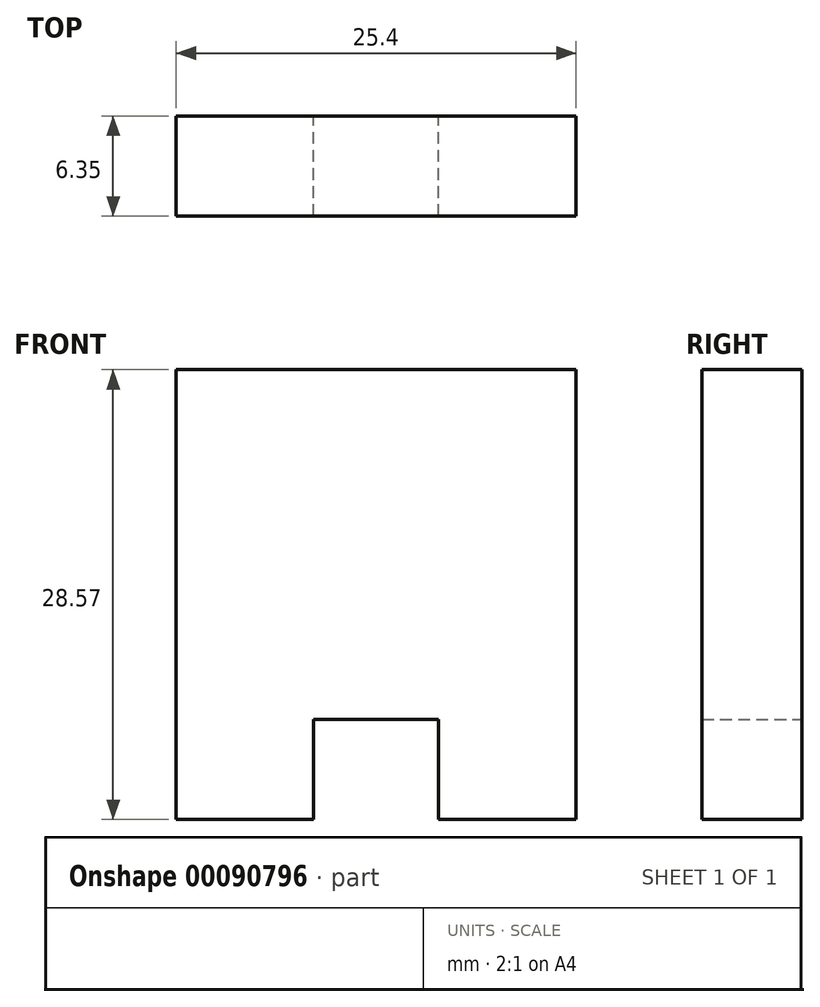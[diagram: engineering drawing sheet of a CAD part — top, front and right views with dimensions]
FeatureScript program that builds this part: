
annotation { "Feature Type Name" : "Feature", "Feature Type Description" : "" }
export const myFeature = defineFeature(function(context is Context, id is Id, definition is map)
    precondition{}
    {
        {
            var Q0;
            Q0=qCreatedBy(makeId("Front.planeOp"),FACE);
            var sketch = newSketch(context, id + "F0", { "sketchPlane" : qUnion([Q0])});
            skLineSegment(sketch, "E0.bottom", {"start": v(0, 0) * mm, "end": v(25.4, 0) * mm});
            skLineSegment(sketch, "E0.top", {"start": v(0, -28.57) * mm, "end": v(25.4, -28.57) * mm});
            skLineSegment(sketch, "E0.left", {"start": v(0, 0) * mm, "end": v(0, -28.57) * mm});
            skLineSegment(sketch, "E0.right", {"start": v(25.4, 0) * mm, "end": v(25.4, -28.57) * mm});
            skLineSegment(sketch, "E1.bottom", {"start": v(12.7, -28.57) * mm, "end": v(8.73, -28.57) * mm});
            skLineSegment(sketch, "E1.top", {"start": v(12.7, -22.22) * mm, "end": v(8.73, -22.22) * mm});
            skLineSegment(sketch, "E1.left", {"start": v(12.7, -28.57) * mm, "end": v(12.7, -22.22) * mm});
            skLineSegment(sketch, "E1.right", {"start": v(8.73, -28.57) * mm, "end": v(8.73, -22.22) * mm});
            skLineSegment(sketch, "E2.MirrorCS", {"start": v(12.7, -22.22) * mm, "end": v(16.67, -22.22) * mm});
            skLineSegment(sketch, "E3.MirrorCS", {"start": v(16.67, -28.57) * mm, "end": v(16.67, -22.22) * mm});
            skLineSegment(sketch, "E4.MirrorCS", {"start": v(12.7, -28.57) * mm, "end": v(16.67, -28.57) * mm});
            skSolve(sketch);
        }
        {
            var Q0;
            Q0=makeQuery(id+"F0.imprint","IMPRINT",FACE,{"disambiguationData":[TD([[makeQuery(id+"F0.imprint","IMPRINT",EDGE,{"derivedFrom":sQuery(id+"F0.wireOp",EDGE,"E0.bottom")}),-1.0]])]});
            extrude(context, id + "F1", {"entities" : qUnion([Q0]), "depth" : 6.35 * mm});
        }
    });
